FCSTD DOCUMENT  (FreeCAD 0.19R24366 (Git))
Label: hullexperiment-1
License: All rights reserved
LicenseURL: http://en.wikipedia.org/wiki/All_rights_reserved
objects: Sketcher::SketchObject×3, Part::FeaturePython×3, App::DocumentObjectGroup×1
note: 6 computed .brp shape members not serialized (recipe doc carries the construction recipe); baked Part::Feature solids carry a one-line shape summary decoded from their .brp

FEATURE [Sketcher::SketchObject] Sketch
  FullyConstrained = true
  Placement = pos=(0,0,0) rot=(1,0,0;1.5708rad)
  sketch-geometry (15):
    g0: LineSegment StartX=0 StartY=166 StartZ=0 EndX=0 EndY=124 EndZ=0
    g1: LineSegment StartX=0 StartY=166 StartZ=0 EndX=0 EndY=208 EndZ=0
    g2: LineSegment StartX=0 StartY=82 StartZ=0 EndX=0 EndY=124 EndZ=0
    g3: LineSegment StartX=0 StartY=82 StartZ=0 EndX=0 EndY=40 EndZ=0
    g4: LineSegment StartX=0 StartY=82 StartZ=0 EndX=72.746 EndY=82 EndZ=0
    g5: LineSegment StartX=0 StartY=124 StartZ=0 EndX=145.492 EndY=124 EndZ=0
    g6: LineSegment StartX=0 StartY=166 StartZ=0 EndX=184.425 EndY=166 EndZ=0
    g7: LineSegment StartX=0 StartY=208 StartZ=0 EndX=193.989 EndY=208 EndZ=0
    g8: Circle CenterX=96.9947 CenterY=208 CenterZ=0 NormalX=0 NormalY=0 NormalZ=1 AngleXU=0 Radius=96.9947
    g9: LineSegment StartX=0 StartY=208 StartZ=0 EndX=0 EndY=250 EndZ=0
    g10: LineSegment StartX=0 StartY=250 StartZ=0 EndX=184.425 EndY=250 EndZ=0
    g11: LineSegment StartX=0 StartY=40 StartZ=0 EndX=145.492 EndY=124 EndZ=0
    g12: LineSegment StartX=0 StartY=124 StartZ=0 EndX=0 EndY=166 EndZ=0
    g13: LineSegment StartX=0 StartY=0 StartZ=0 EndX=0 EndY=40 EndZ=0
    g14: LineSegment StartX=0 StartY=82 StartZ=0 EndX=0 EndY=124 EndZ=0
  constraints (44):
    c: PointOnObject(g10,g8)
    c: PointOnObject(g7,g8)
    c: PointOnObject(g5,g8)
    c: PointOnObject(g4,g11)
    c: Coincident(g9,g10)
    c: Coincident(g1,g7)
    c: Coincident(g1,g9)
    c: Coincident(g1,g6)
    c: Coincident(g1,g12)
    c: Coincident(g2,g3)
    c: Coincident(g2,g4)
    c: Coincident(g3,g11)
    c: Coincident(g3,g13)
    c: Vertical(g13)
    c: Vertical(g3)
    c: Vertical(g2)
    c: Vertical(g0)
    c: Vertical(g12)
    c: Vertical(g1)
    c: Vertical(g9)
    c: Coincident(g0,g5)
    c: Horizontal(g4)
    c: Coincident(g-1,g13)
    c: Coincident(g5,g11)
    c: Horizontal(g5)
    c: Tangent(g11,g8)
    c: Horizontal(g6)
    c: Horizontal(g7)
    c: Horizontal(g10)
    c: Coincident(g0,g12)
    c: Equal(g3,g2)
    c: Equal(g2,g0)
    c: Equal(g0,g12)
    c: Equal(g12,g1)
    c: PointOnObject(g1,g8)
    c: Tangent(g1,g8)
    c: DistanceY(g3,g9) = 210
    c: PointOnObject(g6,g8)
    c: Coincident(g14,g2)
    c: Coincident(g14,g0)
    c: Equal(g14,g0)
    c: Vertical(g14)
    c: Equal(g9,g1)
    c: DistanceY(g13,g9) = 250
FEATURE [Part::FeaturePython] Interpolation_Curve  # WARN: FeaturePython — macro-defined, semantics opaque (R4)
  CustomTangents = false
  DetectAligned = false
  Parameters = [0,0.269732,0.539464,0.723361,0.861681,1]
  Parametrization = 0
  Periodic = false
  PointList = -> [Sketch]
  Polygonal = false
  Tangents = (6) [(0.792216,2.69434e-16,0.610241),(0.894901,4.94466e-17,0.446265),(0.804308,1.81954e-16,0.594212),(0.453441,1.04549e-16,0.891286),+2 more]
  Tolerance = 1e-07
  UTurns = 0
  VTurns = 0
  WireOutput = false
FEATURE [Sketcher::SketchObject] MirroredSketch
  ExternalGeometry = -> [Sketch]
  FullyConstrained = false
  Placement = pos=(-100,0,0) rot=(1,0,0;1.5708rad)
  sketch-geometry (15):
    g0: LineSegment StartX=50 StartY=165.786 StartZ=0 EndX=50 EndY=123.652 EndZ=0
    g1: LineSegment StartX=50 StartY=165.786 StartZ=0 EndX=50 EndY=207.919 EndZ=0
    g2: LineSegment StartX=50 StartY=81.5185 StartZ=0 EndX=50 EndY=123.652 EndZ=0
    g3: LineSegment StartX=50 StartY=81.5185 StartZ=0 EndX=50 EndY=39.3849 EndZ=0
    g4: LineSegment StartX=50 StartY=81.5185 StartZ=0 EndX=-22.9775 EndY=81.5185 EndZ=0
    g5: LineSegment StartX=50 StartY=123.652 StartZ=0 EndX=-95.9551 EndY=123.652 EndZ=0
    g6: LineSegment StartX=50 StartY=165.786 StartZ=0 EndX=-135.011 EndY=165.786 EndZ=0
    g7: LineSegment StartX=50 StartY=207.919 StartZ=0 EndX=-144.607 EndY=207.919 EndZ=0
    g8: Circle CenterX=-47.3033 CenterY=207.919 CenterZ=0 NormalX=0 NormalY=0 NormalZ=1 AngleXU=0 Radius=97.3033
    g9: LineSegment StartX=50 StartY=207.919 StartZ=0 EndX=50 EndY=250.053 EndZ=0
    g10: LineSegment StartX=50 StartY=250.053 StartZ=0 EndX=-135.011 EndY=250.053 EndZ=0
    g11: LineSegment StartX=50 StartY=39.3849 StartZ=0 EndX=-95.9551 EndY=123.652 EndZ=0
    g12: LineSegment StartX=50 StartY=123.652 StartZ=0 EndX=50 EndY=165.786 EndZ=0
    g13: LineSegment StartX=50 StartY=0 StartZ=0 EndX=50 EndY=39.3849 EndZ=0
    g14: LineSegment StartX=50 StartY=81.5185 StartZ=0 EndX=50 EndY=123.652 EndZ=0
  constraints (42):
    c: PointOnObject(g10,g8)
    c: PointOnObject(g7,g8)
    c: PointOnObject(g5,g8)
    c: PointOnObject(g4,g11)
    c: Coincident(g9,g10)
    c: Coincident(g1,g7)
    c: Coincident(g1,g9)
    c: Coincident(g1,g6)
    c: Coincident(g1,g12)
    c: Coincident(g2,g3)
    c: Coincident(g2,g4)
    c: Coincident(g3,g11)
    c: Coincident(g3,g13)
    c: Vertical(g13)
    c: Vertical(g3)
    c: Vertical(g2)
    c: Vertical(g0)
    c: Vertical(g12)
    c: Vertical(g1)
    c: Vertical(g9)
    c: Coincident(g0,g5)
    c: Horizontal(g4)
    c: Coincident(g5,g11)
    c: Horizontal(g5)
    c: Tangent(g11,g8)
    c: Horizontal(g6)
    c: Horizontal(g7)
    c: Horizontal(g10)
    c: Coincident(g0,g12)
    c: Equal(g3,g2)
    c: Equal(g2,g0)
    c: Equal(g0,g12)
    c: Equal(g12,g1)
    c: PointOnObject(g1,g8)
    c: Tangent(g1,g8)
    c: PointOnObject(g6,g8)
    c: Coincident(g14,g2)
    c: Coincident(g14,g0)
    c: Equal(g14,g0)
    c: Vertical(g14)
    c: Equal(g9,g1)
    c: DistanceX(g13,g-3) = 50
FEATURE [Sketcher::SketchObject] Sketch004
  FullyConstrained = false
  Placement = pos=(0,0,0) rot=(1,0,0;1.5708rad)
  sketch-geometry (37):
    g0: LineSegment StartX=0 StartY=284.766 StartZ=0 EndX=0 EndY=244.766 EndZ=0
    g1: LineSegment StartX=0 StartY=284.766 StartZ=0 EndX=0 EndY=324.766 EndZ=0
    g2: LineSegment StartX=0 StartY=204.766 StartZ=0 EndX=0 EndY=244.766 EndZ=0
    g3: LineSegment StartX=0 StartY=204.766 StartZ=0 EndX=0 EndY=164.766 EndZ=0
    g4: LineSegment StartX=0 StartY=204.766 StartZ=0 EndX=69.282 EndY=204.766 EndZ=0
    g5: LineSegment StartX=0 StartY=244.766 StartZ=0 EndX=138.564 EndY=244.766 EndZ=0
    g6: LineSegment StartX=0 StartY=284.766 StartZ=0 EndX=175.643 EndY=284.766 EndZ=0
    g7: LineSegment StartX=0 StartY=324.766 StartZ=0 EndX=184.752 EndY=324.766 EndZ=0
    g8: Circle CenterX=92.376 CenterY=324.766 CenterZ=0 NormalX=0 NormalY=0 NormalZ=1 AngleXU=0 Radius=92.376
    g9: LineSegment StartX=0 StartY=324.766 StartZ=0 EndX=0 EndY=364.766 EndZ=0
    g10: LineSegment StartX=0 StartY=364.766 StartZ=0 EndX=175.643 EndY=364.766 EndZ=0
    g11: LineSegment StartX=0 StartY=164.766 StartZ=0 EndX=138.564 EndY=244.766 EndZ=0
    g12: LineSegment StartX=0 StartY=244.766 StartZ=0 EndX=0 EndY=284.766 EndZ=0
    g13: LineSegment StartX=0 StartY=114.766 StartZ=0 EndX=0 EndY=164.766 EndZ=0
    g14: LineSegment StartX=0 StartY=204.766 StartZ=0 EndX=0 EndY=244.766 EndZ=0
    g15: LineSegment StartX=-50 StartY=284.766 StartZ=0 EndX=-50 EndY=244.766 EndZ=0
    g16: LineSegment StartX=-50 StartY=284.766 StartZ=0 EndX=-50 EndY=324.766 EndZ=0
    g17: LineSegment StartX=-50 StartY=204.766 StartZ=0 EndX=-50 EndY=244.766 EndZ=0
    g18: LineSegment StartX=-50 StartY=204.766 StartZ=0 EndX=-50 EndY=164.766 EndZ=0
    g19: LineSegment StartX=-50 StartY=204.766 StartZ=0 EndX=-119.282 EndY=204.766 EndZ=0
    g20: LineSegment StartX=-50 StartY=244.766 StartZ=0 EndX=-188.564 EndY=244.766 EndZ=0
    g21: LineSegment StartX=-50 StartY=284.766 StartZ=0 EndX=-225.643 EndY=284.766 EndZ=0
    g22: LineSegment StartX=-50 StartY=324.766 StartZ=0 EndX=-234.752 EndY=324.766 EndZ=0
    g23: Circle CenterX=-142.376 CenterY=324.766 CenterZ=0 NormalX=0 NormalY=0 NormalZ=1 AngleXU=0 Radius=92.376
    g24: LineSegment StartX=-50 StartY=324.766 StartZ=0 EndX=-50 EndY=364.766 EndZ=0
    g25: LineSegment StartX=-50 StartY=364.766 StartZ=0 EndX=-225.643 EndY=364.766 EndZ=0
    g26: LineSegment StartX=-50 StartY=244.766 StartZ=0 EndX=-50 EndY=284.766 EndZ=0
    g27: LineSegment StartX=-50 StartY=204.766 StartZ=0 EndX=-50 EndY=244.766 EndZ=0
    g28: LineSegment StartX=0 StartY=114.766 StartZ=0 EndX=-50 EndY=114.766 EndZ=0
    g29: LineSegment StartX=-50 StartY=114.766 StartZ=0 EndX=-50 EndY=164.766 EndZ=0
    g30: LineSegment StartX=-188.564 StartY=244.766 StartZ=0 EndX=-50 EndY=164.766 EndZ=0
    g31: LineSegment StartX=-50 StartY=364.766 StartZ=0 EndX=0 EndY=364.766 EndZ=0
    g32: LineSegment StartX=-50 StartY=114.766 StartZ=0 EndX=-50 EndY=49.7664 EndZ=0
    g33: LineSegment StartX=0 StartY=114.766 StartZ=0 EndX=0 EndY=49.7664 EndZ=0
    g34: LineSegment StartX=0 StartY=49.7664 StartZ=0 EndX=-50 EndY=49.7664 EndZ=0
    g35: LineSegment StartX=-50 StartY=49.7664 StartZ=0 EndX=-25 EndY=38.1087 EndZ=0
    g36: LineSegment StartX=-25 StartY=38.1087 StartZ=0 EndX=0 EndY=49.7664 EndZ=0
  constraints (106):
    c: PointOnObject(g10,g8)
    c: PointOnObject(g7,g8)
    c: PointOnObject(g5,g8)
    c: PointOnObject(g4,g11)
    c: Coincident(g9,g10)
    c: Coincident(g1,g7)
    c: Coincident(g1,g9)
    c: Coincident(g1,g6)
    c: Coincident(g1,g12)
    c: Coincident(g2,g3)
    c: Coincident(g2,g4)
    c: Coincident(g3,g11)
    c: Coincident(g3,g13)
    c: Vertical(g13)
    c: Vertical(g3)
    c: Vertical(g2)
    c: Vertical(g0)
    c: Vertical(g12)
    c: Vertical(g1)
    c: Vertical(g9)
    c: Coincident(g0,g5)
    c: Horizontal(g4)
    c: Coincident(g5,g11)
    c: Horizontal(g5)
    c: Tangent(g11,g8)
    c: Horizontal(g6)
    c: Horizontal(g7)
    c: Horizontal(g10)
    c: Coincident(g0,g12)
    c: Equal(g3,g2)
    c: Equal(g2,g0)
    c: Equal(g0,g12)
    c: Equal(g12,g1)
    c: PointOnObject(g1,g8)
    c: Tangent(g1,g8)
    c: DistanceY(g3,g9) = 200
    c: PointOnObject(g6,g8)
    c: Coincident(g14,g2)
    c: Coincident(g14,g0)
    c: Equal(g14,g0)
    c: Vertical(g14)
    c: Equal(g9,g1)
    c: DistanceY(g13,g9) = 250
    c: PointOnObject(g25,g23)
    c: PointOnObject(g22,g23)
    c: PointOnObject(g20,g23)
    c: Coincident(g24,g25)
    c: Coincident(g16,g22)
    c: Coincident(g16,g24)
    c: Coincident(g16,g21)
    c: Coincident(g16,g26)
    c: Coincident(g17,g18)
    c: Coincident(g17,g19)
    c: Vertical(g18)
    c: Vertical(g17)
    c: Vertical(g15)
    c: Vertical(g26)
    c: Vertical(g16)
    c: Vertical(g24)
    c: Coincident(g15,g20)
    c: Horizontal(g19)
    c: Horizontal(g20)
    c: Horizontal(g21)
    c: Horizontal(g22)
    c: Horizontal(g25)
    c: Coincident(g15,g26)
    c: Equal(g18,g17)
    c: Equal(g17,g15)
    c: Equal(g15,g26)
    c: Equal(g26,g16)
    c: PointOnObject(g16,g23)
    c: Tangent(g16,g23)
    c: PointOnObject(g21,g23)
    c: Coincident(g27,g17)
    c: Coincident(g27,g15)
    c: Equal(g27,g15)
    c: Vertical(g27)
    c: Equal(g24,g16)
    c: Equal(g22,g7)
    c: Coincident(g28,g13)
    c: Horizontal(g28)
    c: Coincident(g29,g28)
    c: Coincident(g29,g18)
    c: Vertical(g29)
    c: Coincident(g30,g20)
    c: Coincident(g30,g18)
    c: PointOnObject(g19,g30)
    c: Tangent(g30,g23)
    c: Coincident(g31,g24)
    c: Coincident(g31,g9)
    c: Horizontal(g31)
    c: Coincident(g32,g28)
    c: Vertical(g32)
    c: Coincident(g33,g13)
    c: PointOnObject(g33,g-2)
    c: Vertical(g33)
    c: Coincident(g34,g33)
    c: Coincident(g34,g32)
    c: Horizontal(g34)
    c: DistanceY(g32,g32) = 65
    c: DistanceX(g34,g34) = 50
    c: Coincident(g35,g32)
    c: Coincident(g36,g33)
    c: Angle(g36,g35) = 2.26893
    c: Angle(g35,g34) = 0.436332
    c: Coincident(g35,g36)
FEATURE [Part::FeaturePython] Interpolation_Curve009  # WARN: FeaturePython — macro-defined, semantics opaque (R4)
  CustomTangents = false
  DetectAligned = false
  Parameters = [0,0.138319,0.276639,0.460535,0.730268,1]
  Parametrization = 0
  Periodic = false
  PointList = -> [Sketch004]
  Polygonal = false
  Tangents = (6) [(-0.449624,-1.98334e-16,-0.893218),(0.00181196,-2.22044e-16,-0.999998),(0.453441,-1.97905e-16,-0.891286),(0.804308,-1.31942e-16,-0.594212),+2 more]
  Tolerance = 1e-07
  UTurns = 0
  VTurns = 0
  WireOutput = false
FEATURE [Part::FeaturePython] Interpolation_Curve010  # WARN: FeaturePython — macro-defined, semantics opaque (R4)
  CustomTangents = false
  DetectAligned = false
  Parameters = [0,0.138319,0.276639,0.460535,0.730268,1]
  Parametrization = 0
  Periodic = false
  PointList = -> [Sketch004]
  Polygonal = false
  Tangents = (6) [(0.449624,-1.98334e-16,-0.893218),(-0.00181194,-2.22044e-16,-0.999998),(-0.453441,-1.97905e-16,-0.891286),(-0.804308,-1.31942e-16,-0.594212),+2 more]
  Tolerance = 1e-07
  UTurns = 0
  VTurns = 0
  WireOutput = false
FEATURE [App::DocumentObjectGroup] Group  label="Section1"
  Group = -> [Sketch,Interpolation_Curve,MirroredSketch,Sketch004,Interpolation_Curve009,Interpolation_Curve010]
